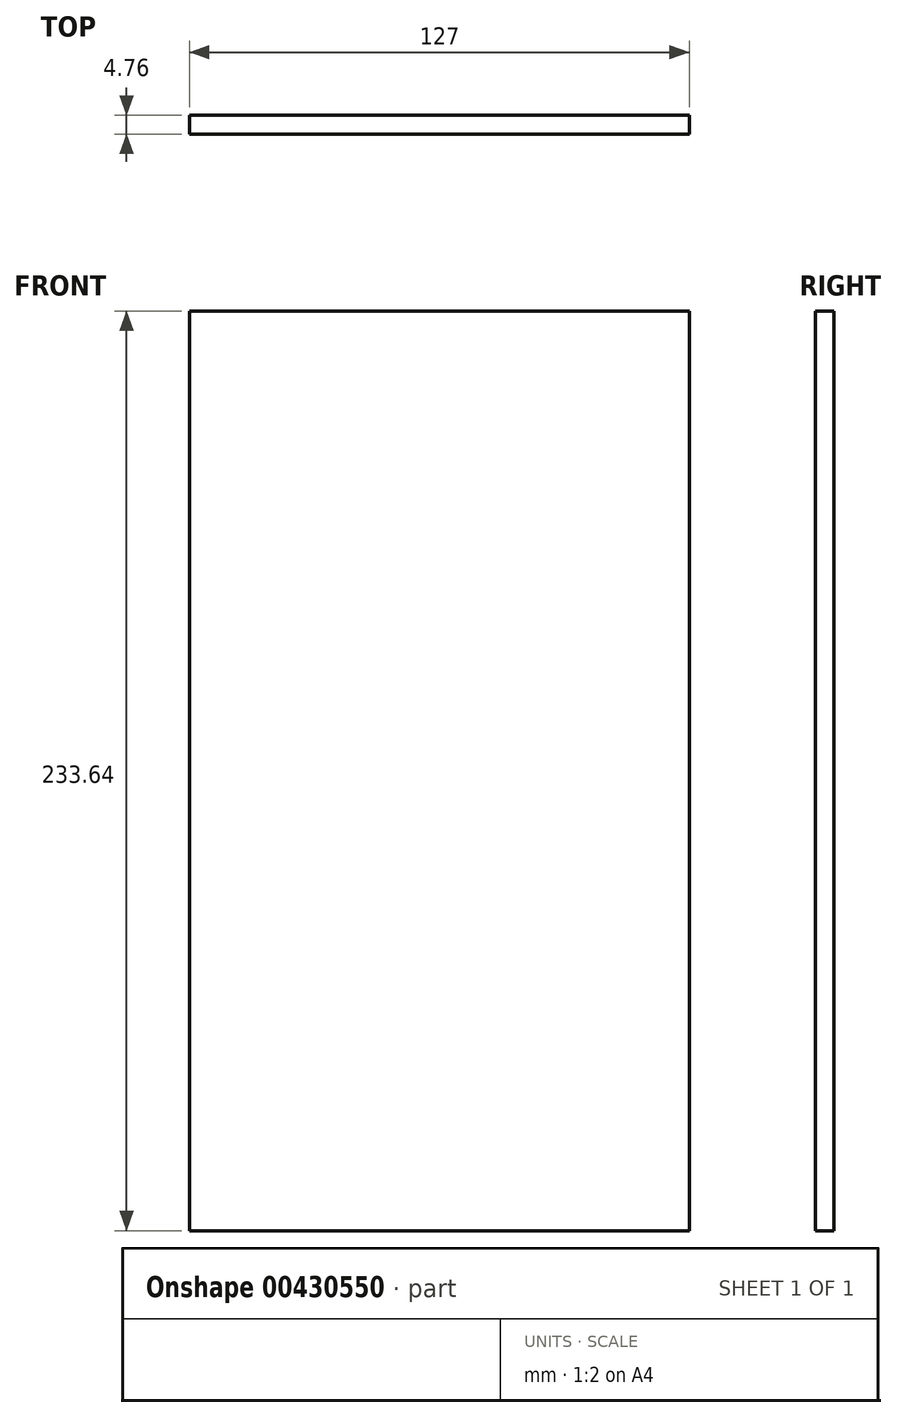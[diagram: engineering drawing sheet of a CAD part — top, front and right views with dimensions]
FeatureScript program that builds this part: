
annotation { "Feature Type Name" : "Feature", "Feature Type Description" : "" }
export const myFeature = defineFeature(function(context is Context, id is Id, definition is map)
    precondition{}
    {
        {
            var Q0;
            Q0=qCreatedBy(makeId("Front.planeOp"),FACE);
            var sketch = newSketch(context, id + "F0", { "sketchPlane" : qUnion([Q0])});
            skLineSegment(sketch, "E0.bottom", {"start": v(-232.36, 201.9) * mm, "end": v(214.22, 201.9) * mm});
            skLineSegment(sketch, "E0.top", {"start": v(-232.36, -179.1) * mm, "end": v(214.22, -179.1) * mm});
            skLineSegment(sketch, "E0.left", {"start": v(-232.36, 201.9) * mm, "end": v(-232.36, -179.1) * mm});
            skLineSegment(sketch, "E0.right", {"start": v(214.22, 201.9) * mm, "end": v(214.22, -179.1) * mm});
            skLineSegment(sketch, "E1.bottom", {"start": v(-56.32, 298.46) * mm, "end": v(70.68, 298.46) * mm});
            skLineSegment(sketch, "E1.top", {"start": v(-56.32, -31.74) * mm, "end": v(70.68, -31.74) * mm});
            skLineSegment(sketch, "E1.left", {"start": v(-56.32, 298.46) * mm, "end": v(-56.32, -31.74) * mm});
            skLineSegment(sketch, "E1.right", {"start": v(70.68, 298.46) * mm, "end": v(70.68, -31.74) * mm});
            skSolve(sketch);
        }
        {
            var Q0;
            {var subQ5=sQuery(id+"F0.wireOp",EDGE,"E1.top");Q0=makeQuery(id+"F0.imprint","IMPRINT",FACE,{"disambiguationData":[TD([[makeQuery(id+"F0.imprint","IMPRINT",EDGE,{"derivedFrom":subQ5}),1.0]])]});}
            extrude(context, id + "F1", {"entities" : qUnion([Q0]), "depth" : 4.76 * mm});
        }
    });
